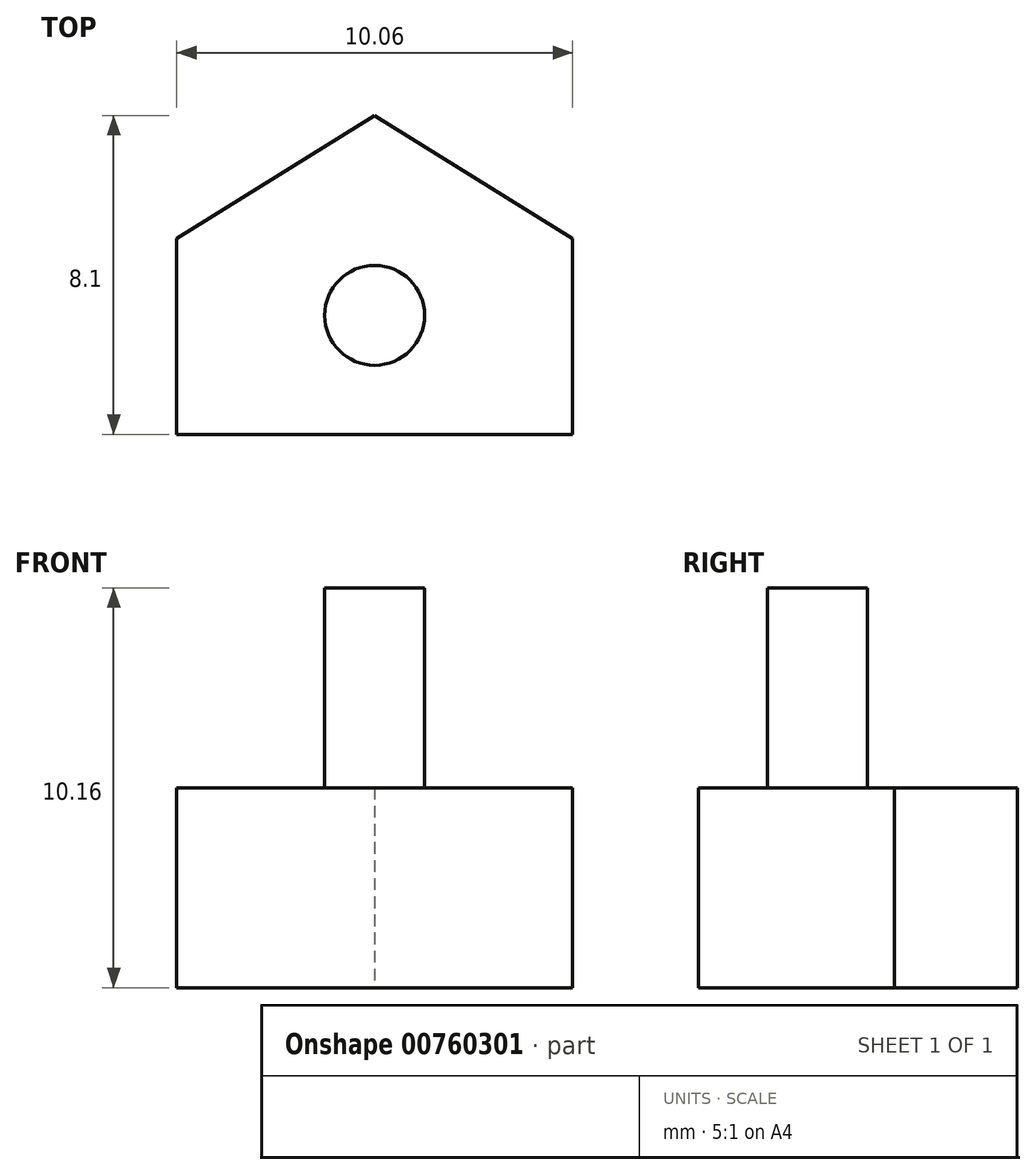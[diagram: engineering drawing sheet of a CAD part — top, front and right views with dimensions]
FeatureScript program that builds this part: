
annotation { "Feature Type Name" : "Feature", "Feature Type Description" : "" }
export const myFeature = defineFeature(function(context is Context, id is Id, definition is map)
    precondition{}
    {
        {
            var Q0;
            Q0=qCreatedBy(makeId("Top.planeOp"),FACE);
            var sketch = newSketch(context, id + "F0", { "sketchPlane" : qUnion([Q0])});
            skLineSegment(sketch, "E0.bottom", {"start": v(0, 0) * mm, "end": v(10.06, 0) * mm});
            skLineSegment(sketch, "E0.left", {"start": v(0, 0) * mm, "end": v(0, 4.98) * mm});
            skLineSegment(sketch, "E0.right", {"start": v(10.06, 0) * mm, "end": v(10.06, 4.98) * mm});
            skLineSegment(sketch, "E1", {"start": v(0, 4.98) * mm, "end": v(5.03, 8.1) * mm});
            skLineSegment(sketch, "E2", {"start": v(5.03, 8.1) * mm, "end": v(10.06, 4.98) * mm});
            skSolve(sketch);
        }
        {
            var Q0;
            Q0 = qSketchRegion(id + "F0", true);
            extrude(context, id + "F1", {"entities" : qUnion([Q0]), "depth" : 5.08 * mm, "offsetDistance" : 25.4 * mm});
        }
        {
            var Q0;
            Q0=makeQuery(id+"F1.opExtrude","CAP_FACE",FACE,{"disambiguationData":[OSD([sQuery(id+"F0.wireOp",EDGE,"E0.bottom"),sQuery(id+"F0.wireOp",EDGE,"E0.left"),sQuery(id+"F0.wireOp",EDGE,"E0.right"),sQuery(id+"F0.wireOp",EDGE,"E1"),sQuery(id+"F0.wireOp",EDGE,"E2")])],"isStart":false});
            var sketch = newSketch(context, id + "F2", { "sketchPlane" : qUnion([Q0])});
            skCircle(sketch, "E3", {"center": v(5.03, 3.02) * mm, "radius": 1.27 * mm});
            skSolve(sketch);
        }
        {
            var Q0;
            Q0 = qSketchRegion(id + "F2", true);
            extrude(context, id + "F3", {"entities" : qUnion([Q0]), "operationType" : NewBodyOperationType.ADD, "depth" : 5.08 * mm, "offsetDistance" : 25.4 * mm});
        }
    });
